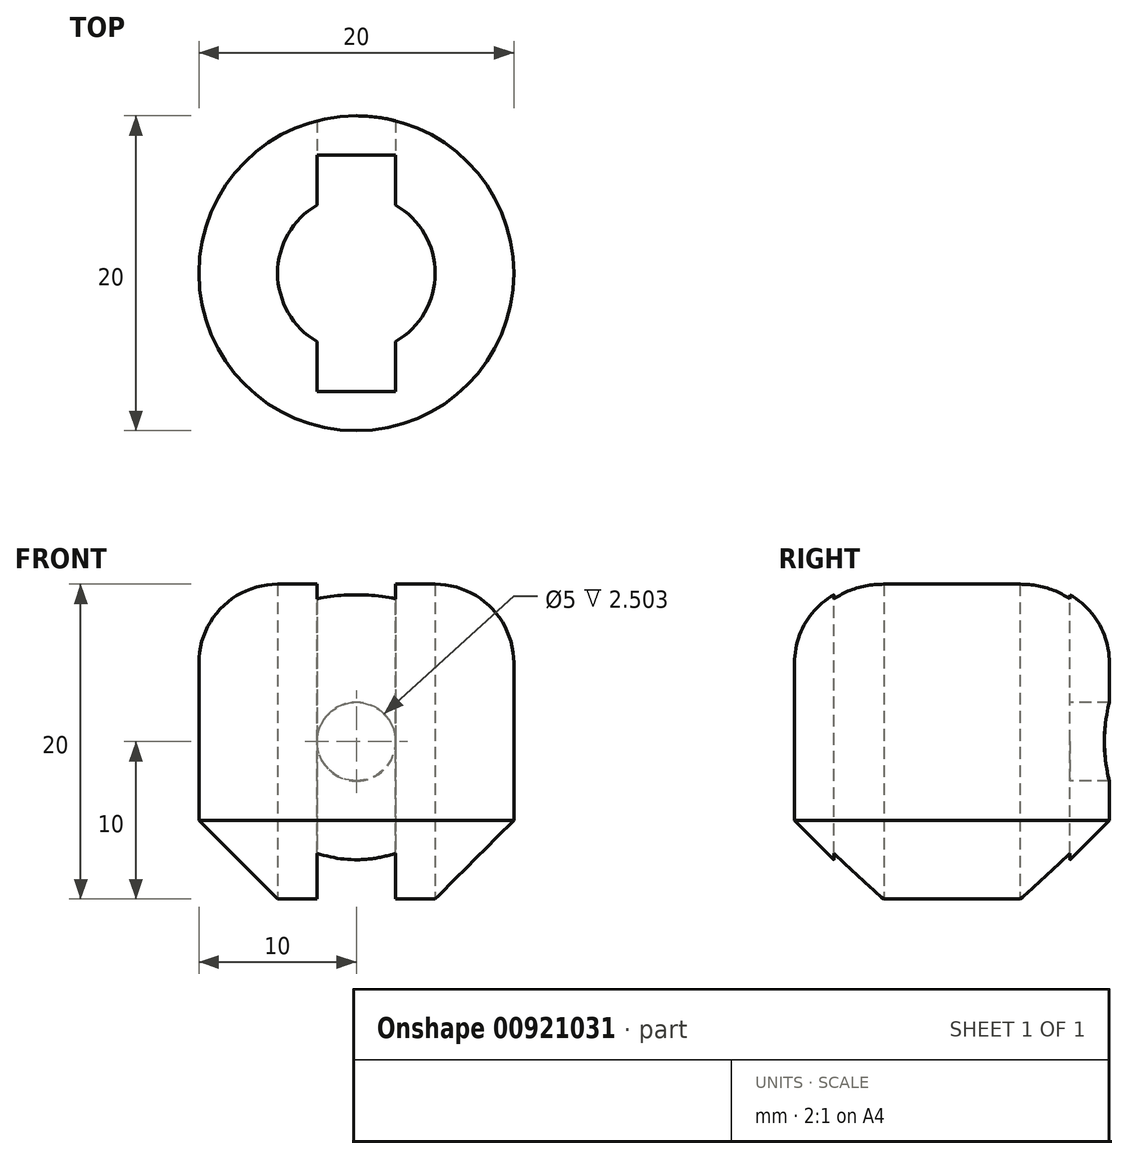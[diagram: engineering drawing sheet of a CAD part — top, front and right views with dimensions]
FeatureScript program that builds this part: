
annotation { "Feature Type Name" : "Feature", "Feature Type Description" : "" }
export const myFeature = defineFeature(function(context is Context, id is Id, definition is map)
    precondition{}
    {
        {
            var Q0;
            Q0=qCreatedBy(makeId("Top.planeOp"),FACE);
            var sketch = newSketch(context, id + "F0", { "sketchPlane" : qUnion([Q0])});
            skCircle(sketch, "E0", {"center": v(0, 0) * mm, "radius": 10 * mm});
            skCircle(sketch, "E1", {"center": v(0, 0) * mm, "radius": 5 * mm});
            skSolve(sketch);
        }
        {
            var Q0;
            Q0=makeQuery(id+"F0.imprint","IMPRINT",FACE,{"disambiguationData":[TD([[makeQuery(id+"F0.imprint","IMPRINT",EDGE,{"derivedFrom":sQuery(id+"F0.wireOp",EDGE,"E0")}),1.0]])]});
            extrude(context, id + "F1", {"entities" : qUnion([Q0]), "endBound" : BoundingType.SYMMETRIC, "depth" : 20 * mm, "offsetDistance" : 25 * mm});
        }
        {
            var Q0;
            Q0=makeQuery(id+"F1.opExtrude","CAP_FACE",FACE,{"disambiguationData":[OSD([sQuery(id+"F0.wireOp",EDGE,"E0"),sQuery(id+"F0.wireOp",EDGE,"E1")])],"isStart":false});
            var sketch = newSketch(context, id + "F2", { "sketchPlane" : qUnion([Q0])});
            skLineSegment(sketch, "E2.bottom", {"start": v(2.5, 7.5) * mm, "end": v(-2.5, 7.5) * mm});
            skLineSegment(sketch, "E2.top", {"start": v(2.5, -7.5) * mm, "end": v(-2.5, -7.5) * mm});
            skLineSegment(sketch, "E2.left", {"start": v(2.5, 7.5) * mm, "end": v(2.5, -7.5) * mm});
            skLineSegment(sketch, "E2.right", {"start": v(-2.5, 7.5) * mm, "end": v(-2.5, -7.5) * mm});
            skPoint(sketch, "E2.middle", {"position": v(0, 0) * mm});
            skSolve(sketch);
        }
        {
            var Q0;
            {var subQ0=sQuery(id+"F2.wireOp",EDGE,"E2.left");var subQ1=makeQuery(id+"F1.opExtrude","CAP_EDGE",EDGE,{"disambiguationData":[OSD([sQuery(id+"F0.wireOp",EDGE,"E1")])],"isStart":false});var subQ2=makeQuery(id+"F2.imprint","INTERSECT",VERTEX,{"disambiguationData":[OD(0.0)],"derivedFrom":[subQ1,subQ0]});Q0=makeQuery(id+"F2.imprint","IMPRINT",FACE,{"disambiguationData":[TD([[makeQuery(id+"F2.imprint","IMPRINT",EDGE,{"disambiguationData":[TD([[subQ2,-1.0]])],"derivedFrom":subQ0}),-1.0]])]});}
            var Q1;
            {var subQ0=sQuery(id+"F2.wireOp",EDGE,"E2.bottom");Q1=makeQuery(id+"F2.imprint","IMPRINT",FACE,{"disambiguationData":[TD([[makeQuery(id+"F2.imprint","IMPRINT",EDGE,{"derivedFrom":subQ0}),1.0]])]});}
            var Q2;
            {var subQ0=sQuery(id+"F2.wireOp",EDGE,"E2.top");Q2=makeQuery(id+"F2.imprint","IMPRINT",FACE,{"disambiguationData":[TD([[makeQuery(id+"F2.imprint","IMPRINT",EDGE,{"derivedFrom":subQ0}),-1.0]])]});}
            var Q3;
            Q3=sQuery(id+"F2.wireOp",EDGE,"E2.left");
            var Q4;
            Q4=sQuery(id+"F2.wireOp",EDGE,"E2.right");
            var Q5;
            Q5=sQuery(id+"F2.wireOp",EDGE,"E2.top");
            var Q6;
            Q6=sQuery(id+"F2.wireOp",EDGE,"E2.bottom");
            extrude(context, id + "F3", {"entities" : qUnion([Q0, Q1, Q2]), "operationType" : NewBodyOperationType.REMOVE, "surfaceEntities" : qUnion([Q3, Q4, Q5, Q6]), "oppositeDirection" : true, "depth" : 25 * mm, "offsetDistance" : 25 * mm});
        }
        {
            var Q0;
            Q0=makeQuery(id+"F1.opExtrude","CAP_EDGE",EDGE,{"disambiguationData":[OSD([sQuery(id+"F0.wireOp",EDGE,"E0")])],"isStart":false});
            fillet(context, id + "F4", {"entities" : qUnion([Q0]), "radius" : 5 * mm, "tangentPropagation" : true, "allowEdgeOverflow" : false});
        }
        {
            var Q0;
            Q0=makeQuery(id+"F1.opExtrude","CAP_EDGE",EDGE,{"disambiguationData":[OSD([sQuery(id+"F0.wireOp",EDGE,"E0")])],"isStart":true});
            chamfer(context, id + "F5", {"entities" : qUnion([Q0]), "chamferType" : ChamferType.TWO_OFFSETS, "width1" : 5 * mm, "oppositeDirection" : false, "width2" : 5 * mm, "tangentPropagation" : true});
        }
        {
            var Q0;
            Q0=qCreatedBy(makeId("Front.planeOp"),FACE);
            var sketch = newSketch(context, id + "F6", { "sketchPlane" : qUnion([Q0])});
            skPoint(sketch, "E3", {"position": v(0, 0) * mm});
            skSolve(sketch);
        }
        {
            var Q0;
            Q0=sQuery(id+"F6.wireOp",VERTEX,"E3");
            var Q1;
            Q1=makeQuery(id+"F1.opExtrude","SWEPT_BODY",BODY,{"disambiguationData":[OSD([sQuery(id+"F0.wireOp",EDGE,"E0"),sQuery(id+"F0.wireOp",EDGE,"E1")])]});
            hole(context, id + "F7", {"style" : HoleStyle.SIMPLE, "endStyle" : HoleEndStyle.THROUGH, "holeDiameter" : 5 * mm, "majorDiameter" : 5 * mm, "isTappedThrough" : true, "tappedDepth" : 12 * mm, "tapClearance" : 3, "locations" : qUnion([Q0]), "scope" : qUnion([Q1])});
        }
    });
